# Revit family: VLGFP1002-xxxSW8xxBxxxx
name_source: partatom
category: Oprawy oświetleniowe
revit_build: Autodesk Revit 2017 (Build: 20190508_0315(x64)
units: mm (PartAtom-declared; Revit-internal decimal feet)

## family parameters
Numer OmniClass = 23.80.70.11
Obiekt nadrzędny = Powierzchnia
Punkt obliczania pomieszczeń = Nie
Tnij formami wycięć po wczytaniu = Nie
Typ części = Normalny
Tytuł OmniClass = Luminaries for Internal Lighting
Współdzielony = Nie
Wymiar okrągłego złącza = Użyj średnicy
Źródło światła = Tak

## types (16) — shared parameters
Emituj kształt widoczny w renderingu = Nie
Emituj z długości prostokąta = 63 mm  [stored 0.206693 ft]
Emituj z szerokości prostokąta = 969 mm
Filtr koloru = 16777215
Kod zespołu = D5020200
Lampa = LED
Odchylenie kierunku = 90.00°
Plik sieci fotometrycznej = VLGFP1501-5NDWS840B0800.IES
Producent = RIDI Leuchten GmbH
URL = www.ridi.de
Zmiana temperatury barwowej przyciemniania lampy = <Brak>
brand = RIDI
conformity mark = CE
electrical safety class = 1
height = 66 mm  [stored 0.216535 ft]
ingress protection (IP) code = IP54
length = 1000 mm  [stored 3.28084 ft]
nominal frequency = 50-60Hz
nominal voltage = 230
voltage type (AC, DC, UC) = AC
weight = 1.6 kg
width = 67 mm
zero-valued in all types: Domyślna rzędna

## per-type parameters (varying)
| type | Model | Obciążenie pozorne | rated input power |
| VLGFP1002-5NDSW830B0950 | 1551033SW | 66 VA | 66 |
| VLGFP1002-7DASW830B0950 | 1561033SW | 66 VA | 66 |
| VLGFP1002-5NDSW830B1100 | 1551093SW | 81 VA | 81 |
| VLGFP1002-7DASW830B1100 | 1561093SW | 81 VA | 81 |
| VLGFP1002-5NDSW840B1000 | 1551013SW | 66 VA | 66 |
| VLGFP1002-7DASW840B1000 | 1561013SW | 66 VA | 66 |
| VLGFP1002-5NDSW840B1200 | 1551089SW | 81 VA | 81 |
| VLGFP1002-7DASW840B1200 | 1561089SW | 81 VA | 81 |
| VLGFP1002-5NDSW850B1000 | 1551046SW | 66 VA | 66 |
| VLGFP1002-7DASW850B1000 | 1561046SW | 66 VA | 66 |
| VLGFP1002-5NDSW850B1200 | 1551095SW | 81 VA | 81 |
| VLGFP1002-7DASW850B1200 | 1561095SW | 81 VA | 81 |
| VLGFP1002-5NDSW865B1000 | 1551059SW | 66 VA | 66 |
| VLGFP1002-7DASW865B1000 | 1561059SW | 66 VA | 66 |
| VLGFP1002-5NDSW865B1200 | 1551099SW | 81 VA | 81 |
| VLGFP1002-7DASW865B1200 | 1561099SW | 66 VA | 66 |

note: column(s) folded — value = type name in every type: product name

note: [stored X ft] marks values corroborated as IEEE doubles in the binary element streams (Revit-internal decimal feet)
